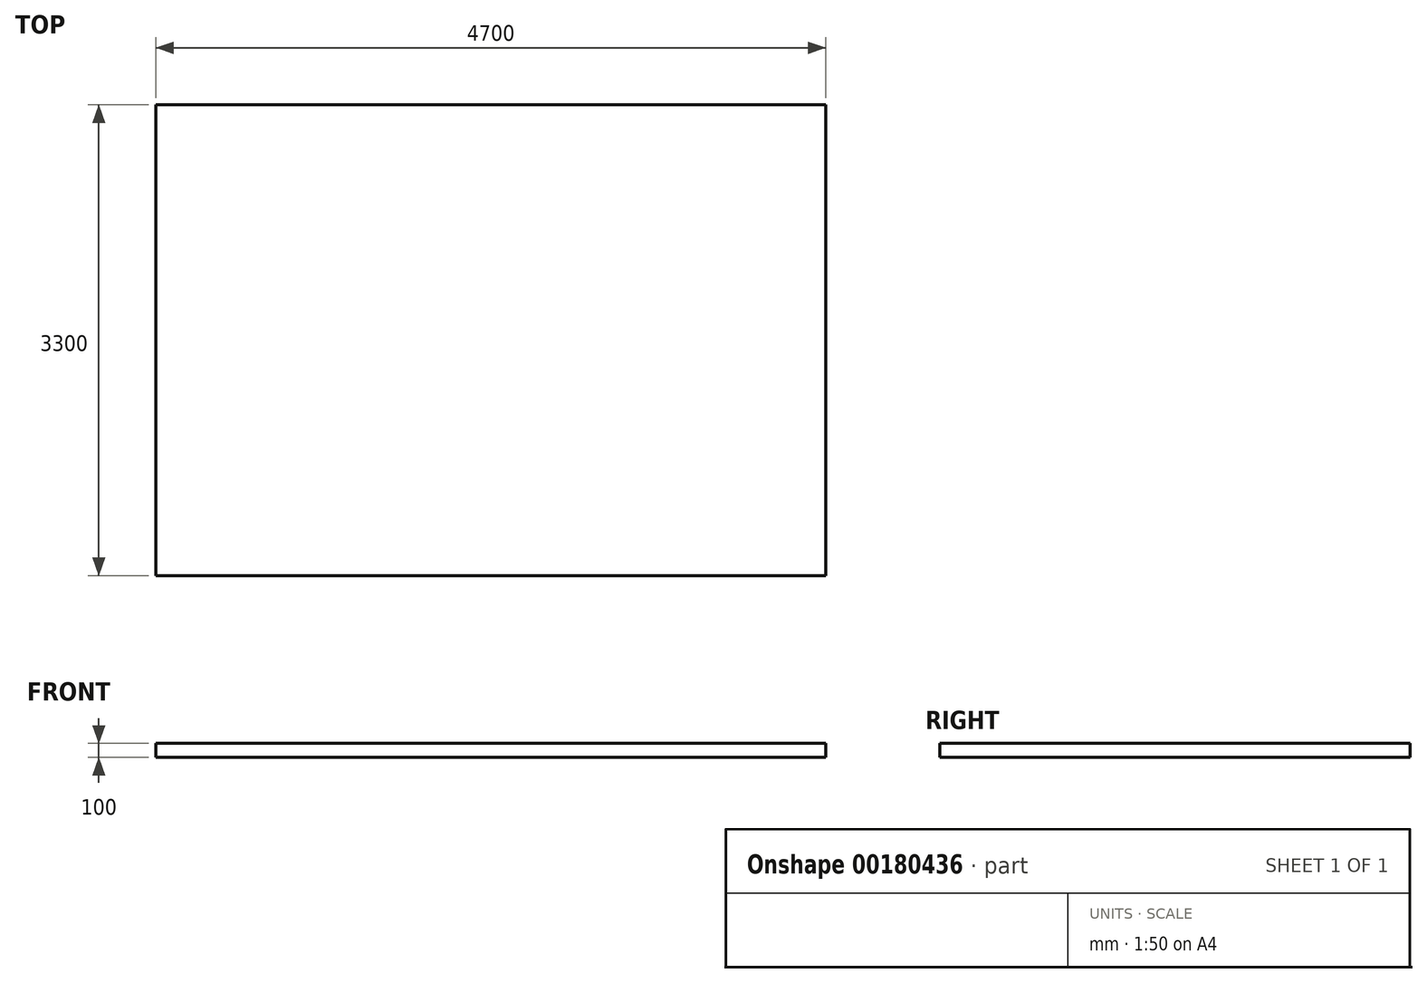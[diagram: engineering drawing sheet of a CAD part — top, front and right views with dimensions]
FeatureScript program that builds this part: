
annotation { "Feature Type Name" : "Feature", "Feature Type Description" : "" }
export const myFeature = defineFeature(function(context is Context, id is Id, definition is map)
    precondition{}
    {
        {
            var Q0;
            Q0=qCreatedBy(makeId("Top.planeOp"),FACE);
            var sketch = newSketch(context, id + "F0", { "sketchPlane" : qUnion([Q0])});
            skLineSegment(sketch, "E0.bottom", {"start": v(-2388.86, 1576.38) * mm, "end": v(2311.14, 1576.38) * mm});
            skLineSegment(sketch, "E0.top", {"start": v(-2388.86, -1723.62) * mm, "end": v(2311.14, -1723.62) * mm});
            skLineSegment(sketch, "E0.left", {"start": v(-2388.86, 1576.38) * mm, "end": v(-2388.86, -1723.62) * mm});
            skLineSegment(sketch, "E0.right", {"start": v(2311.14, 1576.38) * mm, "end": v(2311.14, -1723.62) * mm});
            skSolve(sketch);
        }
        {
            var Q0;
            Q0 = qSketchRegion(id + "F0", true);
            extrude(context, id + "F1", {"entities" : qUnion([Q0]), "depth" : 100 * mm});
        }
    });
